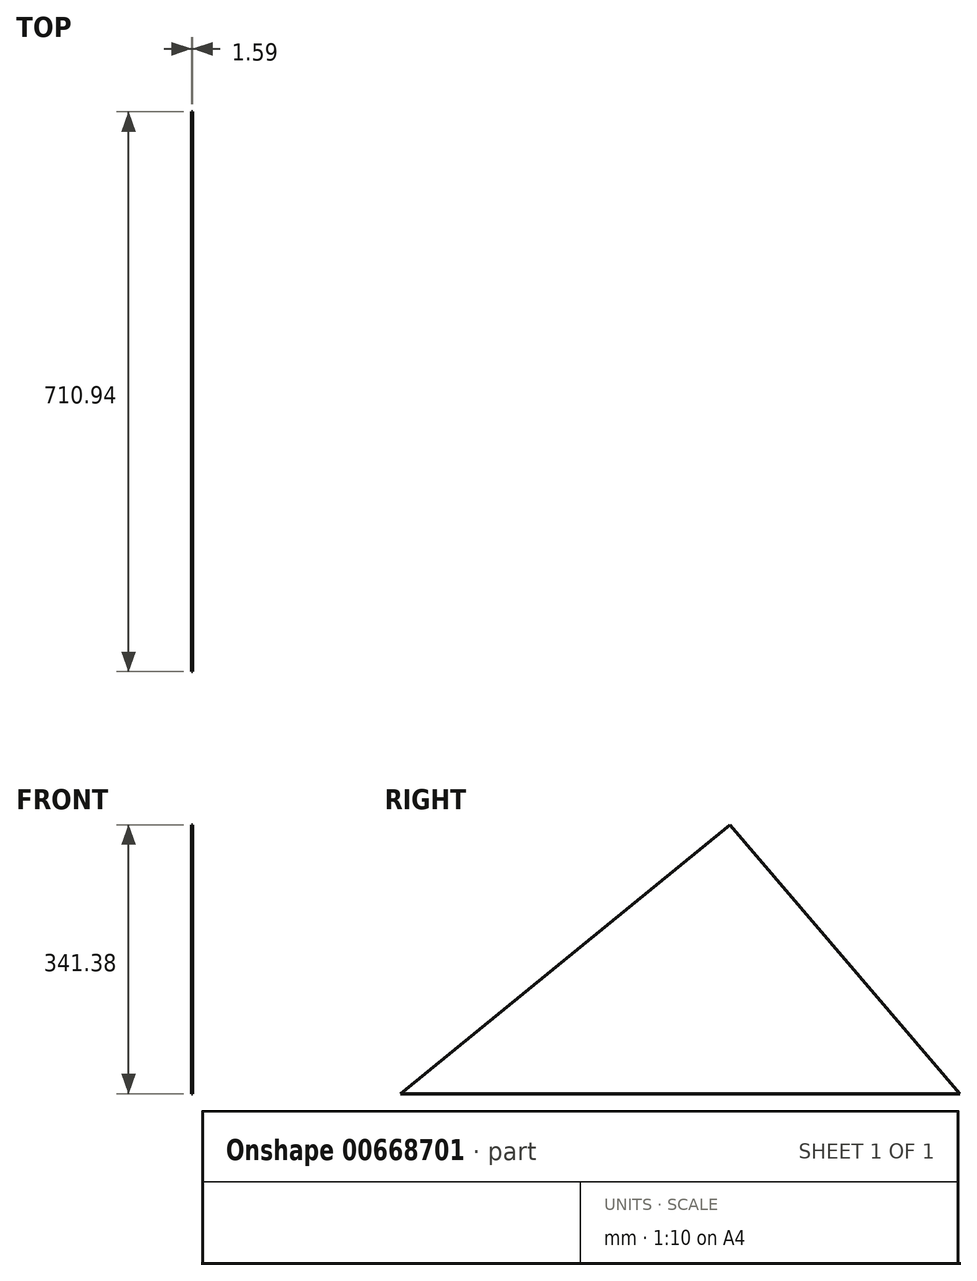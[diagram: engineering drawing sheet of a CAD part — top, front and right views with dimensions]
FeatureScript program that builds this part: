
annotation { "Feature Type Name" : "Feature", "Feature Type Description" : "" }
export const myFeature = defineFeature(function(context is Context, id is Id, definition is map)
    precondition{}
    {
        {
            var Q0;
            Q0=qCreatedBy(makeId("Right.planeOp"),FACE);
            var sketch = newSketch(context, id + "F0", { "sketchPlane" : qUnion([Q0])});
            skLineSegment(sketch, "E0", {"start": v(-338.8, 0) * mm, "end": v(372.15, 0) * mm});
            skLineSegment(sketch, "E1", {"start": v(372.15, 0) * mm, "end": v(79.61, 341.38) * mm});
            skLineSegment(sketch, "E2", {"start": v(79.61, 341.38) * mm, "end": v(-338.8, 0) * mm});
            skSolve(sketch);
        }
        {
            var Q0;
            Q0 = qSketchRegion(id + "F0", true);
            extrude(context, id + "F1", {"entities" : qUnion([Q0]), "depth" : 1.59 * mm, "offsetDistance" : 25.4 * mm});
        }
    });
